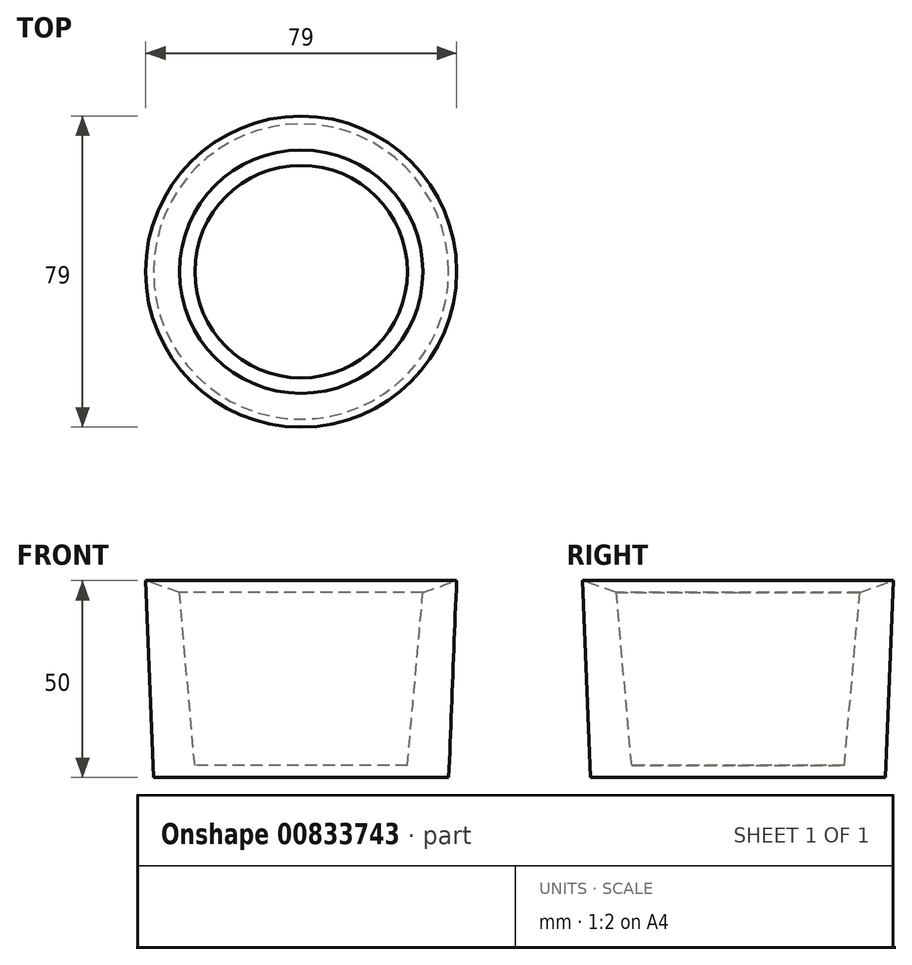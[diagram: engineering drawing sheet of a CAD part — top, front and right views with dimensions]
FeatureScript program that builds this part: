
annotation { "Feature Type Name" : "Feature", "Feature Type Description" : "" }
export const myFeature = defineFeature(function(context is Context, id is Id, definition is map)
    precondition{}
    {
        {
            var Q0;
            Q0=qCreatedBy(makeId("Right.planeOp"),FACE);
            var sketch = newSketch(context, id + "F0", { "sketchPlane" : qUnion([Q0])});
            skLineSegment(sketch, "E0", {"start": v(-39.5, 50) * mm, "end": v(-30.92, 47) * mm});
            skLineSegment(sketch, "E1", {"start": v(-30.92, 47) * mm, "end": v(-27, 3) * mm});
            skLineSegment(sketch, "E2", {"start": v(-27, 3) * mm, "end": v(0, 3) * mm});
            skLineSegment(sketch, "E3", {"start": v(0, 3) * mm, "end": v(0, 0) * mm});
            skLineSegment(sketch, "E4", {"start": v(0, 0) * mm, "end": v(-37.5, 0) * mm});
            skLineSegment(sketch, "E5", {"start": v(-37.5, 0) * mm, "end": v(-39.5, 50) * mm});
            skSolve(sketch);
        }
        {
            var Q0;
            Q0=makeQuery(id+"F0.imprint","IMPRINT",FACE,{"disambiguationData":[TD([[makeQuery(id+"F0.imprint","IMPRINT",EDGE,{"derivedFrom":sQuery(id+"F0.wireOp",EDGE,"E0")}),-1.0]])]});
            var Q1;
            Q1=sQuery(id+"F0.wireOp",EDGE,"E3");
            revolve(context, id + "F1", {"surfaceOperationType" : NewSurfaceOperationType.NEW, "entities" : qUnion([Q0]), "axis" : qUnion([Q1]), "revolveType" : RevolveType.FULL});
        }
    });
